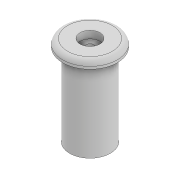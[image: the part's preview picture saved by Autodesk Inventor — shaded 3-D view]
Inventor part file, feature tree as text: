
AUTODESK INVENTOR PART (.ipt)
format: ipt  version: 2022 (Build 260153000, 153)  size: 115,200 bytes
history: native  units: mm
features: extrude x4, sketch x4, fillet x1
ambient origin geometry x8: Origin, YZ Plane, XZ Plane, XY Plane, X Axis, Y Axis, Z Axis, Center Point
bodies: Solid1 (feature_tree)
feature tree (9):
  extrude  "Extrusion1"  Depth=33.0mm TaperAngle=0.0deg
  extrude  "Extrusion2"  Depth=3.0mm TaperAngle=0.0deg
  extrude  "Extrusion3"  Depth=100.0mm TaperAngle=0.0deg
  extrude  "Extrusion4"  Depth=3.0mm TaperAngle=0.0deg
  fillet  "Fillet1"  Radius=2.0mm
  sketch  "Sketch1"  dims[d0=16.4mm d1=33.0mm d2=0.0mm]
  sketch  "Sketch3"  dims[d4=22.0mm d5=3.0mm d6=0.0mm]
  sketch  "Sketch4"  dims[d7=3.2mm d8=100.0mm d9=0.0mm]
  sketch  "Sketch5"  dims[d10=8.0mm d11=3.0mm d12=0.0mm d13=2.0mm]
